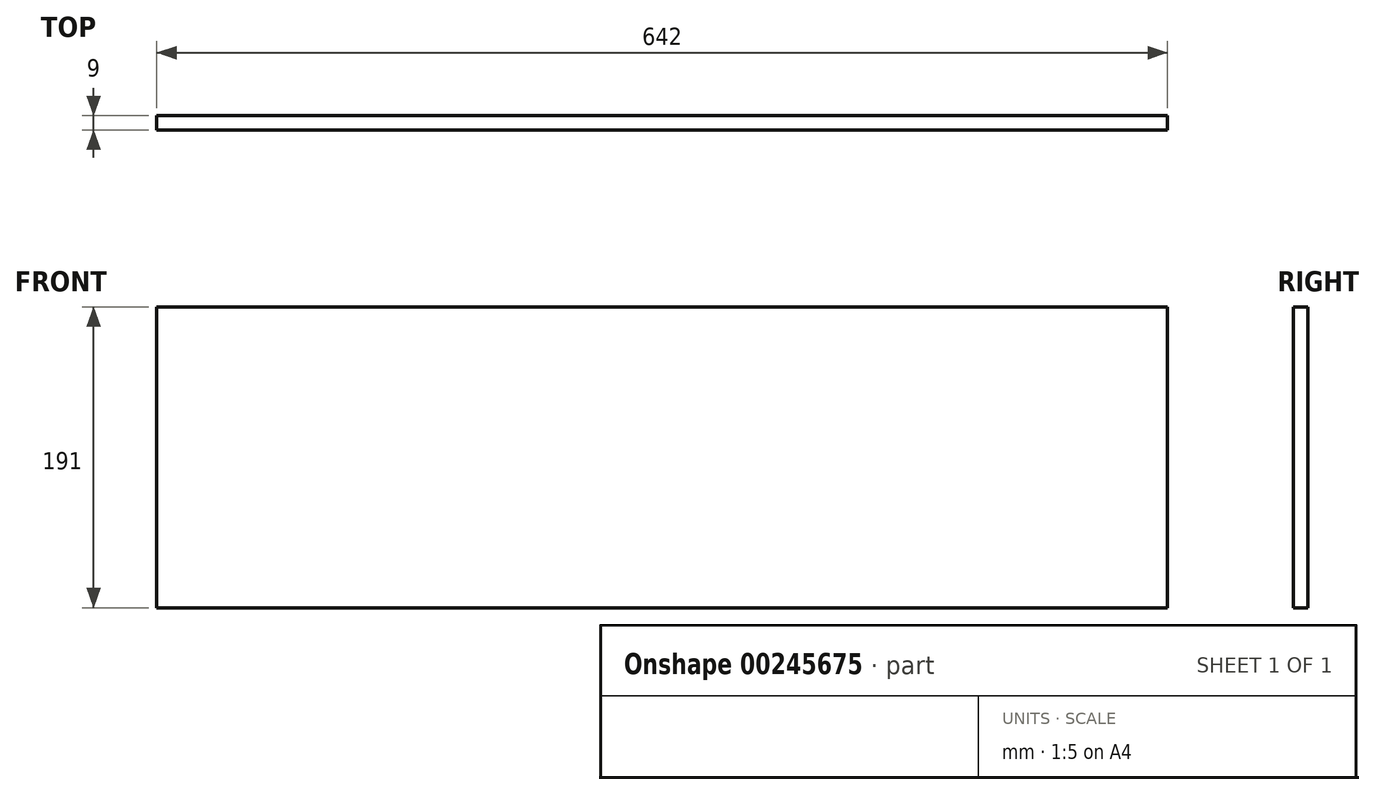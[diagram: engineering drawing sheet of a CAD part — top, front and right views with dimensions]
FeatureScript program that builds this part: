
annotation { "Feature Type Name" : "Feature", "Feature Type Description" : "" }
export const myFeature = defineFeature(function(context is Context, id is Id, definition is map)
    precondition{}
    {
        {
            var Q0;
            Q0=qCreatedBy(makeId("Front.planeOp"),FACE);
            var sketch = newSketch(context, id + "F0", { "sketchPlane" : qUnion([Q0])});
            skLineSegment(sketch, "E0.bottom", {"start": v(321, 95.5) * mm, "end": v(-321, 95.5) * mm});
            skLineSegment(sketch, "E0.top", {"start": v(321, -95.5) * mm, "end": v(-321, -95.5) * mm});
            skLineSegment(sketch, "E0.left", {"start": v(321, 95.5) * mm, "end": v(321, -95.5) * mm});
            skLineSegment(sketch, "E0.right", {"start": v(-321, 95.5) * mm, "end": v(-321, -95.5) * mm});
            skPoint(sketch, "E0.middle", {"position": v(0, 0) * mm});
            skSolve(sketch);
        }
        {
            var Q0;
            Q0 = qSketchRegion(id + "F0", true);
            extrude(context, id + "F1", {"entities" : qUnion([Q0]), "depth" : 9 * mm});
        }
    });
